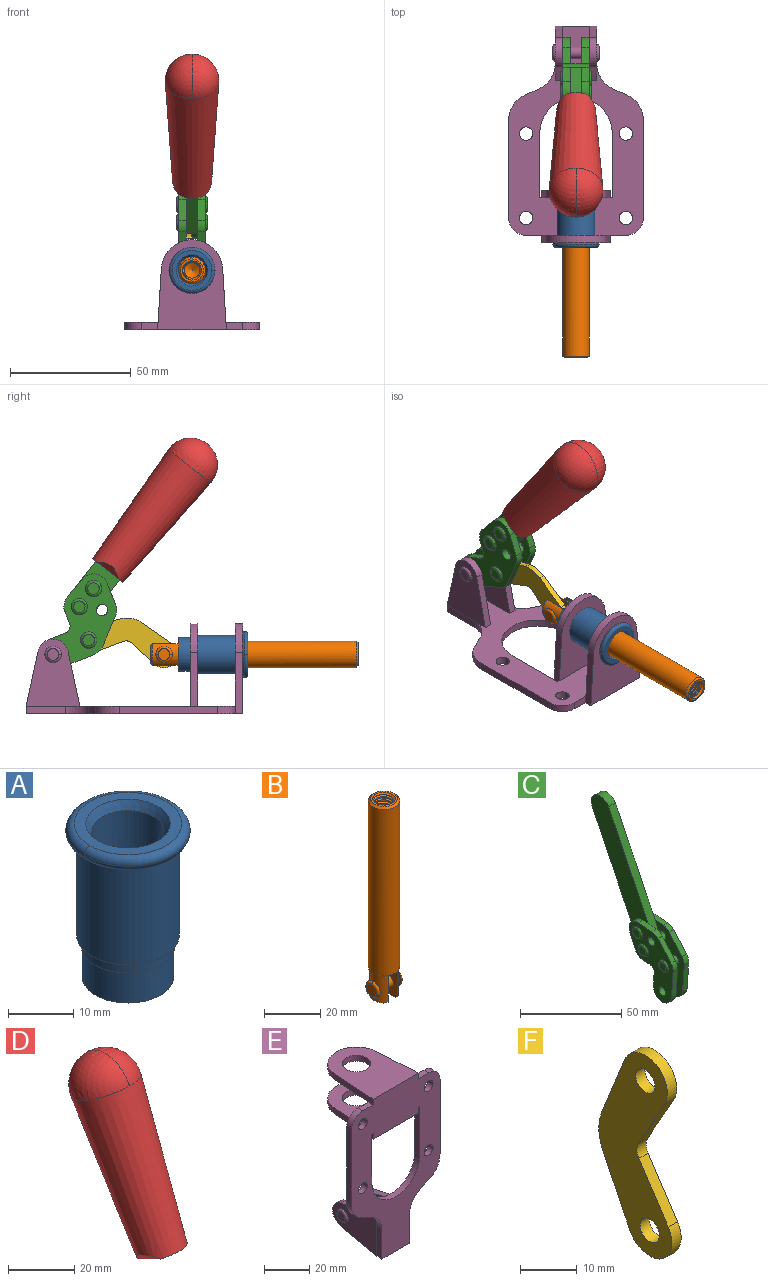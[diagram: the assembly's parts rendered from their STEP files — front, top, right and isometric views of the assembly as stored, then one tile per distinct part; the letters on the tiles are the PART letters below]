
ASSEMBLY  parts=6 mates=6
PART A: 15 faces, bbox 20.6x20.6x28.7 mm
  f0: torus R=8.26mm, axis (0,0,1), area 56.8mm2, adj f1,f10,f12
  f1: torus R=8.26mm, axis (0,0,1), area 56.8mm2, adj f0,f6,f13
  f2: cylinder r=5.59mm len=25.91mm, axis (0,0,1), area 909.6mm2, adj f3,f4
  f3: cone r=6.86mm half-angle=45deg, axis (0,0,-1), area 70.2mm2, adj f2,f14
  f4: cone r=6.47mm half-angle=30deg, axis (0,0,1), area 66.7mm2, adj f2,f13
  f5: cylinder r=7.04mm len=14.07mm, axis (0,0,1), area 252.6mm2, adj f11,f14
  f6: torus R=8.26mm, axis (0,0,1), area 56.8mm2, adj f1,f12,f13
  f7: cylinder r=7.16mm len=14.33mm, axis (0,0,1), area 91.5mm2, adj f9,f11
  f8: cylinder r=7.86mm len=18.42mm, axis (0,0,1), area 909.6mm2, adj f9,f10
  f9: plane 15.72x15.72mm, normal (0,0,-1), area 33mm2, adj f7,f8
  f10: plane 16.51x16.51mm, normal (0,0,-1), area 19.9mm2, adj f0,f8,f12
  f11: plane 14.33x14.33mm, normal (0,0,-1), area 5.7mm2, adj f5,f7
  f12: torus R=8.26mm, axis (0,0,1), area 56.8mm2, adj f0,f6,f10
  f13: plane 16.51x16.51mm, normal (0,0,1), area 82.7mm2, adj f1,f4,f6
  f14: plane 14.07x14.07mm, normal (0,0,-1), area 7.8mm2, adj f3,f5
PART B: 48 faces, bbox 12.6x11.1x86.1 mm
  f0: torus R=2.41mm, axis (-1,0,0), area 15mm2, adj f30,f32,f34
  f1: torus R=2.41mm, axis (-1,0,0), area 15mm2, adj f29,f31,f33
  f2: cylinder r=5.54mm len=72.39mm, axis (0,0,1), area 2518.5mm2, adj f3,f4,f42,f43
  f3: cone r=5.54mm half-angle=45deg, axis (0,0,1), area 7.6mm2, adj f2,f5,f41
  f4: cone r=5.54mm half-angle=45deg, axis (0,0,-1), area 34.9mm2, adj f2,f39
  f5: cylinder r=5.08mm len=11.48mm, axis (0,0,1), area 108.3mm2, adj f3,f7,f8,f41
  f6: cylinder r=2.41mm len=4.83mm, axis (-1,0,0), area 71.2mm2, adj f40,f41
  f7: cylinder r=2.41mm len=4.83mm, axis (-1,0,0), area 7.6mm2, adj f5,f34
  f8: cone r=5.08mm half-angle=45deg, axis (0,0,1), area 10.6mm2, adj f5,f37,f41
  f9: cone r=3.98mm half-angle=45deg, axis (0,0,1), area 17.6mm2, adj f27,f39,f45,f46,f47
  f10: cylinder r=2.41mm len=4.83mm, axis (-1,0,0), area 7.6mm2, adj f33,f38
  f11: cylinder r=3.2mm len=6.4mm, axis (0,0,1), area 78.4mm2, adj f12,f28,f44,f45,f47
  f12: cylinder r=3.2mm len=6.4mm, axis (0,0,1), area 10.5mm2, adj f11,f13,f45,f47
  f13: cylinder r=3.2mm len=6.4mm, axis (0,0,1), area 10.5mm2, adj f12,f14,f45,f47
  f14: cylinder r=3.2mm len=6.4mm, axis (0,0,1), area 10.5mm2, adj f13,f15,f45,f47
  f15: cylinder r=3.2mm len=6.4mm, axis (0,0,1), area 10.5mm2, adj f14,f16,f45,f47
  f16: cylinder r=3.2mm len=6.4mm, axis (0,0,1), area 10.5mm2, adj f15,f17,f45,f47
  f17: cylinder r=3.2mm len=6.4mm, axis (0,0,1), area 10.5mm2, adj f16,f18,f45,f47
  f18: cylinder r=3.2mm len=6.4mm, axis (0,0,1), area 10.5mm2, adj f17,f19,f45,f47
  f19: cylinder r=3.2mm len=6.4mm, axis (0,0,1), area 10.5mm2, adj f18,f20,f45,f47
  f20: cylinder r=3.2mm len=6.4mm, axis (0,0,1), area 10.5mm2, adj f19,f21,f45,f47
  f21: cylinder r=3.2mm len=6.4mm, axis (0,0,1), area 10.5mm2, adj f20,f22,f45,f47
  f22: cylinder r=3.2mm len=6.4mm, axis (0,0,1), area 10.5mm2, adj f21,f23,f45,f47
  f23: cylinder r=3.2mm len=6.4mm, axis (0,0,1), area 10.5mm2, adj f22,f24,f45,f47
  f24: cylinder r=3.2mm len=6.4mm, axis (0,0,1), area 10.5mm2, adj f23,f25,f45,f47
  f25: cylinder r=3.2mm len=6.4mm, axis (0,0,1), area 10.5mm2, adj f24,f26,f45,f47
  f26: cylinder r=3.2mm len=6.4mm, axis (0,0,1), area 10.5mm2, adj f25,f27,f45,f47
  f27: cylinder r=3.2mm len=6.4mm, axis (0,0,1), area 7.4mm2, adj f9,f26,f45,f47
  f28: cone r=3.2mm half-angle=60deg, axis (0,0,1), area 37.2mm2, adj f11
  f29: plane 4.83x4.83mm, normal (-1,0,0), area 18.3mm2, adj f1,f31
  f30: plane 4.83x4.83mm, normal (1,0,0), area 18.3mm2, adj f0,f32
  f31: torus R=2.41mm, axis (-1,0,0), area 15mm2, adj f1,f29,f33
  f32: torus R=2.41mm, axis (-1,0,0), area 15mm2, adj f0,f30,f34
  f33: plane 6.83x6.83mm, normal (1,0,0), area 18.3mm2, adj f1,f10,f31
  f34: plane 6.83x6.83mm, normal (-1,0,0), area 18.3mm2, adj f0,f7,f32
  f35: cone r=5.08mm half-angle=45deg, axis (0,0,1), area 10.6mm2, adj f36,f38,f40
  f36: plane 7.25x1.97mm, normal (0,0,-1), area 10mm2, adj f35,f40
  f37: plane 7.25x1.97mm, normal (0,0,-1), area 10mm2, adj f8,f41
  f38: cylinder r=5.08mm len=11.48mm, axis (0,0,1), area 108.3mm2, adj f10,f35,f40,f42
  f39: plane 9.55x9.55mm, normal (0,0,1), area 22mm2, adj f4,f9
  f40: plane 12.76x10.09mm, normal (1,0,0), area 95.7mm2, adj f6,f35,f36,f38,f42,f43
  f41: plane 12.76x10.09mm, normal (-1,0,0), area 95.7mm2, adj f3,f5,f6,f8,f37,f43
  f42: cone r=5.54mm half-angle=45deg, axis (0,0,1), area 7.6mm2, adj f2,f38,f40
  f43: plane 11.07x4.7mm, normal (0,0,-1), area 50.4mm2, adj f2,f40,f41
  f44: plane 0.89x0.62mm, normal (-1,0,0), area 0.3mm2, adj f11,f45,f46,f47
  f45: bspline ~24.8x7.63mm, area 266.6mm2, adj f9,f11,f12,f13,f14,f15,f16,f17
  f46: bspline ~24.87x7.63mm, area 73.6mm2, adj f9,f44,f45,f47
  f47: bspline ~24.98x7.63mm, area 272.5mm2, adj f9,f11,f12,f13,f14,f15,f16,f17
PART C: 59 faces, bbox 12.9x60.2x99.6 mm
  f0: torus R=2.39mm, axis (-1,0,0), area 14.9mm2, adj f20,f43,f51
  f1: torus R=2.39mm, axis (-1,0,0), area 14.9mm2, adj f19,f42,f51
  f2: torus R=2.39mm, axis (-1,0,0), area 14.9mm2, adj f18,f35,f51
  f3: torus R=2.39mm, axis (-1,0,0), area 14.9mm2, adj f14,f17,f23
  f4: torus R=2.39mm, axis (-1,0,0), area 14.9mm2, adj f13,f16,f23
  f5: torus R=2.39mm, axis (-1,0,0), area 14.9mm2, adj f12,f15,f23
  f6: cylinder r=2.39mm len=4.78mm, axis (1,0,0), area 46.5mm2, adj f48,f50,f51
  f7: cylinder r=2.39mm len=4.78mm, axis (1,0,0), area 46.5mm2, adj f50,f51
  f8: cylinder r=6.35mm len=12.68mm, axis (1,0,0), area 61.8mm2, adj f38,f39,f50,f51
  f9: cylinder r=2.39mm len=4.78mm, axis (-1,0,0), area 70.5mm2, adj f46,f50
  f10: cylinder r=2.39mm len=4.78mm, axis (-1,0,0), area 46.5mm2, adj f23,f45,f46
  f11: cylinder r=2.39mm len=4.78mm, axis (-1,0,0), area 46.5mm2, adj f23,f46
  f12: plane 4.78x4.78mm, normal (1,0,0), area 17.9mm2, adj f5,f15
  f13: plane 4.78x4.78mm, normal (1,0,0), area 17.9mm2, adj f4,f16
  f14: plane 4.78x4.78mm, normal (1,0,0), area 17.9mm2, adj f3,f17
  f15: torus R=2.39mm, axis (-1,0,0), area 14.9mm2, adj f5,f12,f23
  f16: torus R=2.39mm, axis (-1,0,0), area 14.9mm2, adj f4,f13,f23
  f17: torus R=2.39mm, axis (-1,0,0), area 14.9mm2, adj f3,f14,f23
  f18: plane 4.78x4.78mm, normal (-1,0,0), area 17.9mm2, adj f2,f35
  f19: plane 4.78x4.78mm, normal (-1,0,0), area 17.9mm2, adj f1,f42
  f20: plane 4.78x4.78mm, normal (-1,0,0), area 17.9mm2, adj f0,f43
  f21: plane 2.26x0.2mm, normal (1,0,0), area 0.2mm2, adj f31,f44
  f22: plane 2.26x0.2mm, normal (-1,0,0), area 0.2mm2, adj f41,f44
  f23: plane 39.37x30.77mm, normal (1,0,0), area 565.5mm2, adj f3,f4,f5,f10,f11,f15,f16,f17
  f24: cylinder r=6.1mm len=4.15mm, axis (-1,0,0), area 14.7mm2, adj f23,f25,f32,f46
  f25: plane 10.25x9.01mm, normal (0,-0.75,0.66), area 42.3mm2, adj f23,f24,f26,f46
  f26: cylinder r=6.35mm len=4.64mm, axis (-1,0,0), area 15.6mm2, adj f23,f25,f27,f46
  f27: plane 15.84x3.1mm, normal (0,-1,-0.07), area 49.2mm2, adj f23,f26,f28,f46
  f28: cylinder r=6.35mm len=12.68mm, axis (-1,0,0), area 61.8mm2, adj f23,f27,f29,f46
  f29: plane 8.11x3.1mm, normal (0,1,0.07), area 25.2mm2, adj f23,f28,f30,f46
  f30: cylinder r=3.05mm len=3.25mm, axis (-1,0,0), area 14.8mm2, adj f23,f29,f31,f46
  f31: plane 5.99x3.1mm, normal (0,0.07,-1), area 18.6mm2, adj f21,f23,f30,f44,f46
  f32: plane 9.5x3.1mm, normal (0,-0.07,1), area 29.5mm2, adj f23,f24,f33,f46,f47
  f33: cylinder r=6.1mm len=8.63mm, axis (-1,0,0), area 39.1mm2, adj f23,f32,f34,f47
  f34: plane 8.65x3.96mm, normal (0,0.91,-0.42), area 29.5mm2, adj f23,f33,f44,f47
  f35: torus R=2.39mm, axis (-1,0,0), area 14.9mm2, adj f2,f18,f51
  f36: plane 10.25x9.01mm, normal (0,-0.75,0.66), area 42.3mm2, adj f37,f49,f50,f51
  f37: cylinder r=6.35mm len=4.64mm, axis (1,0,0), area 15.6mm2, adj f36,f38,f50,f51
  f38: plane 15.84x3.1mm, normal (0,-1,-0.07), area 49.2mm2, adj f8,f37,f50,f51
  f39: plane 8.11x3.1mm, normal (0,1,0.07), area 25.2mm2, adj f8,f40,f50,f51
  f40: cylinder r=3.05mm len=3.25mm, axis (1,0,0), area 14.8mm2, adj f39,f41,f50,f51
  f41: plane 5.99x3.1mm, normal (0,0.07,-1), area 18.6mm2, adj f22,f40,f44,f50,f51
  f42: torus R=2.39mm, axis (-1,0,0), area 14.9mm2, adj f1,f19,f51
  f43: torus R=2.39mm, axis (-1,0,0), area 14.9mm2, adj f0,f20,f51
  f44: cylinder r=6.35mm len=12.12mm, axis (-1,0,0), area 128.9mm2, adj f21,f22,f23,f31,f34,f41,f46,f47
  f45: plane 2.65x1.35mm, normal (1,0,0), area 1mm2, adj f10,f55
  f46: plane 39.08x20.42mm, normal (-1,0,0), area 412.5mm2, adj f9,f10,f11,f24,f25,f26,f27,f28
  f47: plane 77.62x39.82mm, normal (1,0,0), area 850mm2, adj f32,f33,f34,f44,f53,f54,f55
  f48: plane 2.65x1.35mm, normal (-1,0,0), area 1mm2, adj f6,f55
  f49: cylinder r=6.1mm len=4.15mm, axis (1,0,0), area 14.7mm2, adj f36,f50,f51,f56
  f50: plane 39.08x20.42mm, normal (1,0,0), area 412.5mm2, adj f6,f7,f8,f9,f36,f37,f38,f39
  f51: plane 39.37x30.77mm, normal (-1,0,0), area 565.5mm2, adj f0,f1,f2,f6,f7,f8,f35,f36
  f52: plane 8.65x3.96mm, normal (0,0.91,-0.42), area 29.5mm2, adj f44,f51,f57,f58
  f53: plane 68.49x33.4mm, normal (0,0.9,-0.44), area 358.1mm2, adj f44,f47,f54,f58
  f54: cylinder r=6.35mm len=12.06mm, axis (1,0,0), area 93.7mm2, adj f47,f53,f55,f58
  f55: plane 68.49x33.4mm, normal (0,-0.9,0.44), area 358.1mm2, adj f44,f45,f46,f47,f48,f50,f54,f58
  f56: plane 9.5x3.1mm, normal (0,-0.07,1), area 29.5mm2, adj f49,f50,f51,f57,f58
  f57: cylinder r=6.1mm len=8.63mm, axis (1,0,0), area 39.1mm2, adj f51,f52,f56,f58
  f58: plane 77.62x39.82mm, normal (-1,0,0), area 850mm2, adj f44,f52,f53,f54,f55,f56,f57
PART D: 11 faces, bbox 22.3x42.6x64.5 mm
  f0: sphere r=11.13mm, area 411.4mm2, adj f1,f8
  f1: cone r=11.11mm half-angle=3.3deg, axis (0,0.44,0.9), area 3251.8mm2, adj f0,f7,f8,f9,f10
  f2: cylinder r=6.16mm len=11.7mm, axis (1,0,0), area 89.5mm2, adj f3,f4,f5,f6
  f3: plane 60.23x36.75mm, normal (-1,0,0), area 763.6mm2, adj f2,f4,f6,f10
  f4: plane 51.37x25.05mm, normal (0,0.9,-0.44), area 264.2mm2, adj f2,f3,f5,f10
  f5: plane 60.23x36.75mm, normal (1,0,0), area 763.6mm2, adj f2,f4,f6,f10
  f6: plane 51.37x25.05mm, normal (0,-0.9,0.44), area 264.2mm2, adj f2,f3,f5,f10
  f7: plane 9.95x5.95mm, normal (0.71,-0.31,-0.64), area 25.8mm2, adj f1,f10
  f8: sphere r=11.13mm, area 411.4mm2, adj f0,f1
  f9: plane 9.95x5.95mm, normal (-0.71,-0.31,-0.64), area 25.8mm2, adj f1,f10
  f10: plane 14.27x11.38mm, normal (0,-0.44,-0.9), area 106.7mm2, adj f1,f3,f4,f5,f6,f7,f9
PART E: 55 faces, bbox 55.7x37.4x89.8 mm
  f0: torus R=2.41mm, axis (-1,0,0), area 15mm2, adj f11,f15,f25
  f1: torus R=2.41mm, axis (-1,0,0), area 15mm2, adj f10,f12,f22
  f2: cylinder r=2.78mm len=5.56mm, axis (0,-1,0), area 54.2mm2, adj f30,f54
  f3: cylinder r=14.99mm len=29.97mm, axis (0,-1,0), area 145.9mm2, adj f30,f49,f53,f54
  f4: cylinder r=2.78mm len=5.56mm, axis (0,-1,0), area 54.2mm2, adj f30,f54
  f5: cylinder r=2.78mm len=5.56mm, axis (0,-1,0), area 54.2mm2, adj f30,f54
  f6: cylinder r=2.78mm len=5.56mm, axis (0,-1,0), area 54.2mm2, adj f30,f54
  f7: cylinder r=6.35mm len=12.7mm, axis (0,0,1), area 123.6mm2, adj f27,f51
  f8: cylinder r=6.35mm len=12.7mm, axis (0,0,-1), area 124.7mm2, adj f21,f35
  f9: cylinder r=2.41mm len=11.18mm, axis (-1,0,0), area 169.4mm2, adj f16,f19
  f10: plane 4.83x4.83mm, normal (1,0,0), area 18.3mm2, adj f1,f12
  f11: plane 4.83x4.83mm, normal (-1,0,0), area 18.3mm2, adj f0,f15
  f12: torus R=2.41mm, axis (-1,0,0), area 15mm2, adj f1,f10,f22
  f13: cylinder r=6.35mm len=12.41mm, axis (1,0,0), area 53.4mm2, adj f18,f19,f22,f23
  f14: cylinder r=6.35mm len=12.41mm, axis (-1,0,0), area 53.4mm2, adj f16,f17,f24,f25
  f15: torus R=2.41mm, axis (-1,0,0), area 15mm2, adj f0,f11,f25
  f16: plane 27.86x22.35mm, normal (1,0,0), area 425.4mm2, adj f9,f14,f17,f24,f30
  f17: plane 22.86x4.97mm, normal (0,0.21,0.98), area 72.5mm2, adj f14,f16,f25,f30
  f18: plane 22.86x4.97mm, normal (0,0.21,0.98), area 72.5mm2, adj f13,f19,f22,f30
  f19: plane 27.86x22.35mm, normal (-1,0,0), area 425.4mm2, adj f9,f13,f18,f23,f30
  f20: cylinder r=12.7mm len=25.35mm, axis (0,0,-1), area 119.8mm2, adj f21,f34,f35,f36
  f21: plane 34.21x28.07mm, normal (0,0,-1), area 702.4mm2, adj f8,f20,f30,f34,f36
  f22: plane 27.96x22.45mm, normal (1,0,0), area 407.2mm2, adj f1,f12,f13,f18,f23,f30,f42,f43
  f23: plane 22.86x4.97mm, normal (0,0.21,-0.98), area 72.5mm2, adj f13,f19,f22,f44
  f24: plane 22.86x4.97mm, normal (0,0.21,-0.98), area 72.5mm2, adj f14,f16,f25,f44
  f25: plane 27.86x22.35mm, normal (-1,0,0), area 407.1mm2, adj f0,f14,f15,f17,f24,f30,f45,f46
  f26: plane 3.1x0.95mm, normal (0,0,-1), area 2.7mm2, adj f30,f49,f50,f54
  f27: plane 34.21x28.07mm, normal (0,0,1), area 702.4mm2, adj f7,f28,f30,f50,f52
  f28: cylinder r=12.7mm len=25.35mm, axis (0,0,1), area 118.8mm2, adj f27,f50,f51,f52
  f29: plane 3.1x0.95mm, normal (0,0,-1), area 2.7mm2, adj f30,f52,f53,f54
  f30: plane 86.54x55.63mm, normal (0,1,0), area 2362.9mm2, adj f2,f3,f4,f5,f6,f16,f17,f18
  f31: plane 40.56x3.1mm, normal (-1,0,0), area 125.7mm2, adj f30,f32,f48,f54
  f32: cylinder r=7.11mm len=7.11mm, axis (0,-1,0), area 34.6mm2, adj f30,f31,f33,f54
  f33: plane 6.67x3.1mm, normal (0,0,1), area 20.4mm2, adj f30,f32,f34,f54
  f34: plane 25.39x3.13mm, normal (-1,0.06,0), area 79.5mm2, adj f20,f21,f33,f35,f54
  f35: plane 37.31x28.45mm, normal (0,0,1), area 789.9mm2, adj f8,f20,f34,f36,f54
  f36: plane 25.39x3.13mm, normal (1,0.06,0), area 79.5mm2, adj f20,f21,f35,f37,f54
  f37: plane 6.67x3.1mm, normal (0,0,1), area 20.4mm2, adj f30,f36,f38,f54
  f38: cylinder r=7.11mm len=7.11mm, axis (0,-1,0), area 34.6mm2, adj f30,f37,f39,f54
  f39: plane 40.56x3.1mm, normal (1,0,0), area 125.7mm2, adj f30,f38,f40,f54
  f40: cylinder r=11.18mm len=10.16mm, axis (0,-1,0), area 39.5mm2, adj f30,f39,f41,f54
  f41: plane 6.09x3.1mm, normal (0.42,0,-0.91), area 20.8mm2, adj f30,f40,f42,f54
  f42: cylinder r=11.18mm len=9.41mm, axis (0,-1,0), area 37.2mm2, adj f22,f30,f41,f43,f54
  f43: plane 16.5x3.1mm, normal (1,0,0), area 51.1mm2, adj f22,f42,f44,f54
  f44: plane 17.37x3.1mm, normal (0,0,-1), area 53.8mm2, adj f23,f24,f30,f43,f45,f54
  f45: plane 16.5x3.1mm, normal (-1,0,0), area 51.1mm2, adj f25,f44,f46,f54
  f46: cylinder r=11.18mm len=9.41mm, axis (0,-1,0), area 37.2mm2, adj f25,f30,f45,f47,f54
  f47: plane 6.09x3.1mm, normal (-0.42,0,-0.91), area 20.8mm2, adj f30,f46,f48,f54
  f48: cylinder r=11.18mm len=10.16mm, axis (0,-1,0), area 39.5mm2, adj f30,f31,f47,f54
  f49: plane 26.54x3.1mm, normal (-1,0,0), area 82.3mm2, adj f3,f26,f30,f54
  f50: plane 25.39x3.1mm, normal (1,0.06,0), area 78.8mm2, adj f26,f27,f28,f51,f54
  f51: plane 37.31x28.45mm, normal (0,0,-1), area 789.9mm2, adj f7,f28,f50,f52,f54
  f52: plane 25.39x3.1mm, normal (-1,0.06,0), area 78.8mm2, adj f27,f28,f29,f51,f54
  f53: plane 26.54x3.1mm, normal (1,0,0), area 82.3mm2, adj f3,f29,f30,f54
  f54: plane 89.66x55.63mm, normal (0,-1,0), area 2678.5mm2, adj f2,f3,f4,f5,f6,f26,f29,f31
PART F: 12 faces, bbox 2.3x18.2x42.8 mm
  f0: cylinder r=2.4mm len=4.8mm, axis (1,0,0), area 34.9mm2, adj f4,f11
  f1: cylinder r=10.41mm len=8.47mm, axis (1,0,0), area 20.2mm2, adj f4,f9,f10,f11
  f2: cylinder r=3.05mm len=3.16mm, axis (1,0,0), area 7.7mm2, adj f4,f6,f7,f11
  f3: cylinder r=2.4mm len=4.8mm, axis (1,0,0), area 34.9mm2, adj f4,f11
  f4: plane 42.81x18.23mm, normal (-1,0,0), area 414.1mm2, adj f0,f1,f2,f3,f5,f6,f7,f8
  f5: cylinder r=5.54mm len=10.67mm, axis (1,0,0), area 41.8mm2, adj f4,f6,f10,f11
  f6: plane 11.66x6.53mm, normal (0,-0.87,-0.49), area 30.9mm2, adj f2,f4,f5,f11
  f7: plane 11.17x7.33mm, normal (0,-0.84,0.55), area 30.9mm2, adj f2,f4,f8,f11
  f8: cylinder r=5.54mm len=10.51mm, axis (1,0,0), area 41.8mm2, adj f4,f7,f9,f11
  f9: plane 13.67x6.67mm, normal (0,0.9,-0.44), area 35.1mm2, adj f1,f4,f8,f11
  f10: plane 14.1x5.7mm, normal (0,0.93,0.37), area 35.1mm2, adj f1,f4,f5,f11
  f11: plane 42.81x18.23mm, normal (1,0,0), area 414.1mm2, adj f0,f1,f2,f3,f5,f6,f7,f8
PLACE A rot(axis=(1,0,0),90deg) t=(0,9.8,0)mm
PLACE B rot(axis=(1,0,0),90deg) t=(0,11.07,0)mm
PLACE C rot(axis=(1,0,0),64.1deg) t=(0,1.91,16.46)mm
PLACE D rot(axis=(1,0,0),64.1deg) t=(0.04,1.91,16.46)mm
PLACE E rot(axis=(1,0,0),90deg) t=(0,9.43,0)mm fixed
PLACE F rot(axis=(0,-0.65,-0.76),180deg) t=(-1.16,15.23,3.85)mm
MATE revolute F.f3 <-> B.f6  axis (1,0,0) through (0,-4.41,24.61)mm
MATE revolute E.f0 <-> C.f7  axis (-1,0,0) through (0,41.52,24.61)mm
MATE slider E.f7 <-> B.f2  axis (0,-1,0) through (0,-36.96,24.61)mm
MATE fastened D.f2 <-> C.f54  axis (-1,0,0) through (2.35,-16.4,104.28)mm
MATE revolute F.f0 <-> C.f4  axis (1,0,0) through (0,26.79,30.52)mm
MATE fastened E.f7 <-> A.f1  axis (0,-1,0) through (0,-36.96,24.61)mm
